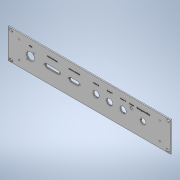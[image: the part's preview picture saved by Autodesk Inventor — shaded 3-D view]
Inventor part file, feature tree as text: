
AUTODESK INVENTOR PART (.ipt)
format: ipt  version: 2022.2 (Build 262287010, 287A)  size: 1,648,128 bytes
history: native  units: mm
features: extrude x3, sketch x2, projected_geometry x1
ambient origin geometry x8: Origin, YZ Plane, XZ Plane, XY Plane, X Axis, Y Axis, Z Axis, Center Point
bodies: Volumenkörper1 (feature_tree)
feature tree (6):
  extrude  "Extrusion1"  Depth=88.1mm
  sketch  "Skizze4"  dims[d6=7.5mm d7=10.4mm d8=38.1mm d9=232.5mm d10=3.4mm d11=208.683mm d12=26.542mm d13=3.0mm d14=0.0mm d15=23.6mm d16=3.1mm d17=19.0mm d18=24.0mm d19=175.0mm d20=1.745329mm d21=1.745329mm d22=10.0mm d23=23.52mm d24=23.52mm d25=3.1mm d26=2.5mm d27=41.521mm d28=110.0mm d29=1.745329mm d30=1.745329mm d31=11.2mm d32=16.66mm d33=16.66mm d34=3.1mm d35=2.5mm d36=28.2mm d37=45.0mm d38=18.0mm d39=8.2mm d40=2.1mm d41=2.1mm d42=18.0mm d43=8.2mm d44=2.1mm d45=2.1mm d46=18.0mm d47=8.2mm d48=2.1mm d49=2.1mm d50=20.0mm d53=8.0mm d55=17.0mm d56=0.0mm d57=0.0mm d58=25.0mm d59=5.0mm d60=10.0mm d61=5.0mm d62=5.0mm d63=5.0mm d64=5.0mm d65=5.0mm d66=5.0mm d67=5.0mm d68=0.5mm d69=0.0mm d70=16.0mm d71=15.0mm d72=1.7mm d73=40.0mm d74=40.0mm d75=25.0mm d76=60.0mm d77=5.0mm]
  extrude  "Extrusion2"  Depth=10.4mm
  extrude  "Extrusion3"  Depth=38.1mm
  sketch  "Skizze3"  dims[d0=482.6mm d1=88.1mm]
  projected_geometry  "Projizierte Kontur1"
